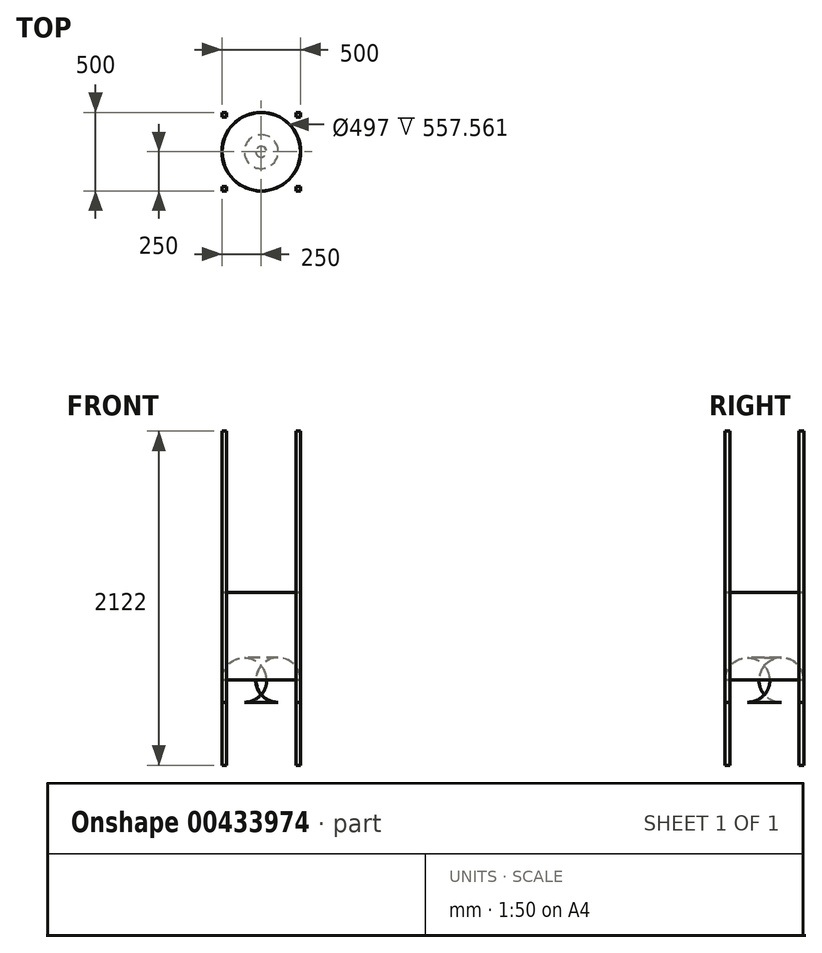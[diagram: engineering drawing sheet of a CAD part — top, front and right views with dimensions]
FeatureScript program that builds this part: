
annotation { "Feature Type Name" : "Feature", "Feature Type Description" : "" }
export const myFeature = defineFeature(function(context is Context, id is Id, definition is map)
    precondition{}
    {
        {
            var Q0;
            Q0=qCreatedBy(makeId("Top.planeOp"),FACE);
            var sketch = newSketch(context, id + "F0", { "sketchPlane" : qUnion([Q0])});
            skCircle(sketch, "E0", {"center": v(0, 0) * mm, "radius": 250 * mm});
            skSolve(sketch);
        }
        {
            var Q0;
            Q0 = qSketchRegion(id + "F0", true);
            extrude(context, id + "F1", {"entities" : qUnion([Q0]), "depth" : 700 * mm});
        }
        {
            var Q0;
            Q0=makeQuery(id+"F1.opExtrude","CAP_EDGE",EDGE,{"disambiguationData":[OSD([sQuery(id+"F0.wireOp",EDGE,"E0")])],"isStart":true});
            fillet(context, id + "F2", {"entities" : qUnion([Q0]), "radius" : 142.44 * mm, "tangentPropagation" : true, "allowEdgeOverflow" : false});
        }
        {
            var Q0;
            Q0=makeQuery(id+"F1.opExtrude","CAP_FACE",FACE,{"disambiguationData":[OSD([sQuery(id+"F0.wireOp",EDGE,"E0")])],"isStart":false});
            shell(context, id + "F3", {"entities" : qUnion([Q0]), "thickness" : 1.5 * mm});
        }
        {
            var Q0;
            {var subQ0=sQuery(id+"F0.wireOp",EDGE,"E0");Q0=makeQuery(id+"F3.opShell","OFFSET_FACE",FACE,{"disambiguationData":[OSD([subQ0]),TDD([makeQuery(id+"F1.opExtrude","CAP_FACE",FACE,{"disambiguationData":[OSD([subQ0])],"isStart":true})])]});}
            var sketch = newSketch(context, id + "F4", { "sketchPlane" : qUnion([Q0])});
            skCircle(sketch, "E1", {"center": v(0, 0) * mm, "radius": 250 * mm, "construction": true});
            skLineSegment(sketch, "E2.bottom", {"start": v(-250, 0) * mm, "end": v(0, 0) * mm});
            skLineSegment(sketch, "E2.right", {"start": v(0, 0) * mm, "end": v(0, -250) * mm});
            skLineSegment(sketch, "E3.bottom", {"start": v(-250, -250) * mm, "end": v(-220, -250) * mm});
            skLineSegment(sketch, "E3.top", {"start": v(-250, -220) * mm, "end": v(-220, -220) * mm});
            skLineSegment(sketch, "E3.left", {"start": v(-250, -250) * mm, "end": v(-250, -220) * mm});
            skLineSegment(sketch, "E3.right", {"start": v(-220, -250) * mm, "end": v(-220, -220) * mm});
            skLineSegment(sketch, "E4.bottom", {"start": v(250, -250) * mm, "end": v(220, -250) * mm});
            skLineSegment(sketch, "E4.top", {"start": v(250, -220) * mm, "end": v(220, -220) * mm});
            skLineSegment(sketch, "E4.left", {"start": v(250, -250) * mm, "end": v(250, -220) * mm});
            skLineSegment(sketch, "E4.right", {"start": v(220, -250) * mm, "end": v(220, -220) * mm});
            skLineSegment(sketch, "E5.bottom", {"start": v(-250, 250) * mm, "end": v(-220, 250) * mm});
            skLineSegment(sketch, "E5.top", {"start": v(-250, 220) * mm, "end": v(-220, 220) * mm});
            skLineSegment(sketch, "E5.left", {"start": v(-250, 250) * mm, "end": v(-250, 220) * mm});
            skLineSegment(sketch, "E5.right", {"start": v(-220, 250) * mm, "end": v(-220, 220) * mm});
            skLineSegment(sketch, "E6.bottom", {"start": v(250, 250) * mm, "end": v(220, 250) * mm});
            skLineSegment(sketch, "E6.top", {"start": v(250, 220) * mm, "end": v(220, 220) * mm});
            skLineSegment(sketch, "E6.left", {"start": v(250, 250) * mm, "end": v(250, 220) * mm});
            skLineSegment(sketch, "E6.right", {"start": v(220, 250) * mm, "end": v(220, 220) * mm});
            skSolve(sketch);
        }
        {
            var Q0;
            Q0 = qSketchRegion(id + "F4", true);
            extrude(context, id + "F5", {"entities" : qUnion([Q0]), "depth" : 1722 * mm});
        }
        {
            var Q0;
            Q0=makeQuery(id+"F5.opExtrude","CAP_FACE",FACE,{"disambiguationData":[OSD([sQuery(id+"F4.wireOp",EDGE,"E3.bottom"),sQuery(id+"F4.wireOp",EDGE,"E3.top"),sQuery(id+"F4.wireOp",EDGE,"E3.left"),sQuery(id+"F4.wireOp",EDGE,"E3.right")])],"isStart":true});
            var Q1;
            Q1=makeQuery(id+"F5.opExtrude","CAP_FACE",FACE,{"disambiguationData":[OSD([sQuery(id+"F4.wireOp",EDGE,"E4.bottom"),sQuery(id+"F4.wireOp",EDGE,"E4.top"),sQuery(id+"F4.wireOp",EDGE,"E4.left"),sQuery(id+"F4.wireOp",EDGE,"E4.right")])],"isStart":true});
            var Q2;
            Q2=makeQuery(id+"F5.opExtrude","CAP_FACE",FACE,{"disambiguationData":[OSD([sQuery(id+"F4.wireOp",EDGE,"E6.bottom"),sQuery(id+"F4.wireOp",EDGE,"E6.top"),sQuery(id+"F4.wireOp",EDGE,"E6.left"),sQuery(id+"F4.wireOp",EDGE,"E6.right")])],"isStart":true});
            var Q3;
            Q3=makeQuery(id+"F5.opExtrude","CAP_FACE",FACE,{"disambiguationData":[OSD([sQuery(id+"F4.wireOp",EDGE,"E5.bottom"),sQuery(id+"F4.wireOp",EDGE,"E5.top"),sQuery(id+"F4.wireOp",EDGE,"E5.left"),sQuery(id+"F4.wireOp",EDGE,"E5.right")])],"isStart":true});
            extrude(context, id + "F6", {"entities" : qUnion([Q0, Q1, Q2, Q3]), "depth" : 400 * mm});
        }
    });
